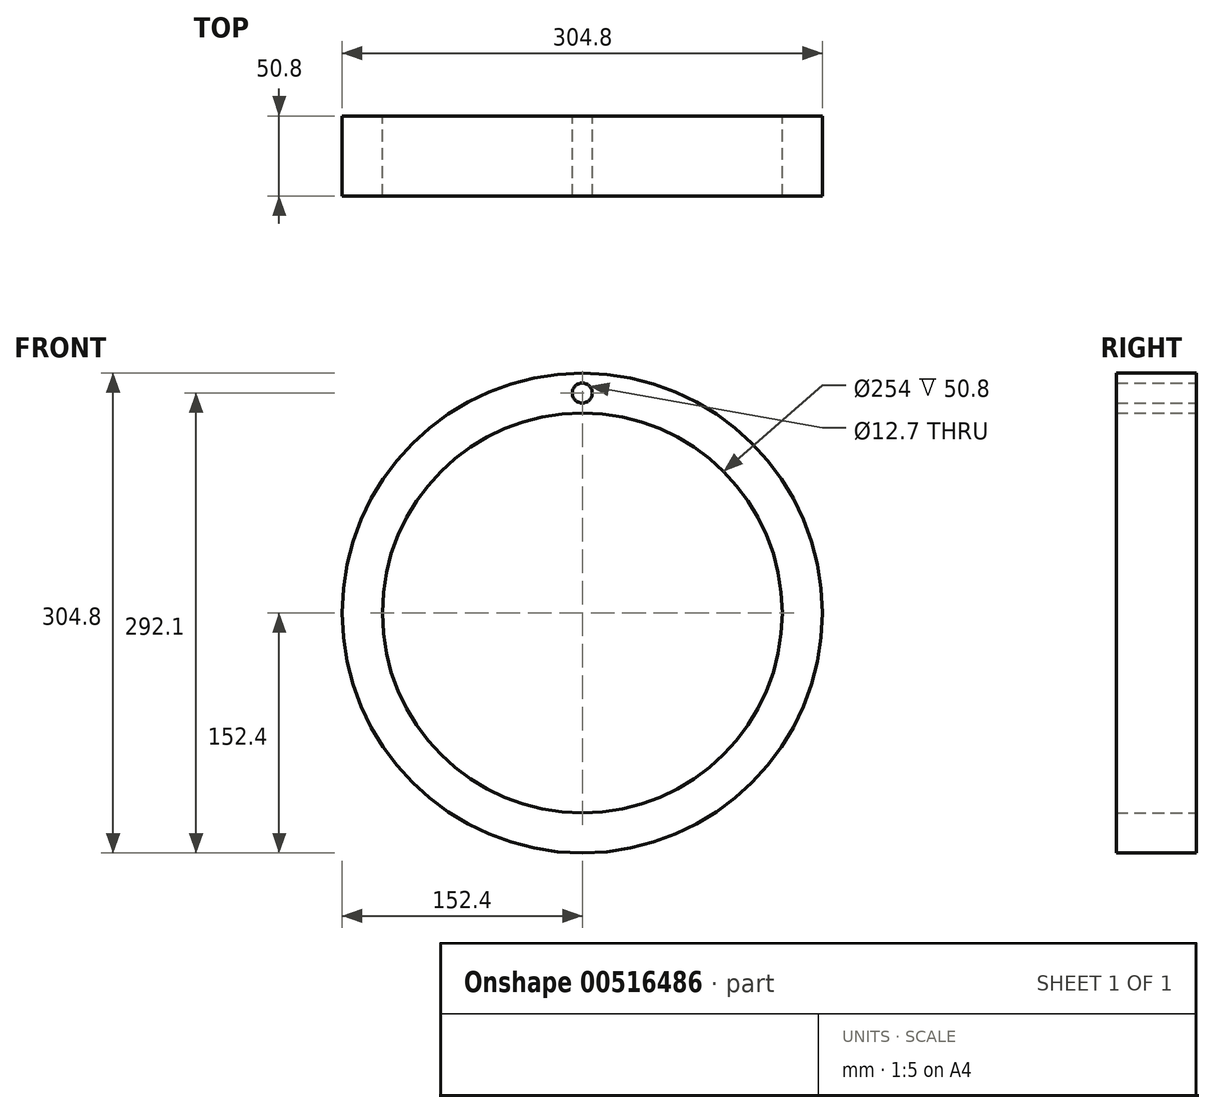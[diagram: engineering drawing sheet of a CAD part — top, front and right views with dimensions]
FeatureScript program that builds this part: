
annotation { "Feature Type Name" : "Feature", "Feature Type Description" : "" }
export const myFeature = defineFeature(function(context is Context, id is Id, definition is map)
    precondition{}
    {
        {
            var Q0;
            Q0=qCreatedBy(makeId("Front.planeOp"),FACE);
            var sketch = newSketch(context, id + "F0", { "sketchPlane" : qUnion([Q0])});
            skCircle(sketch, "E0", {"center": v(0, 0) * mm, "radius": 152.4 * mm});
            skCircle(sketch, "E1", {"center": v(0, 0) * mm, "radius": 127 * mm});
            skCircle(sketch, "E2", {"center": v(0, 139.7) * mm, "radius": 6.35 * mm});
            skSolve(sketch);
        }
        {
            var Q0;
            Q0=makeQuery(id+"F0.imprint","IMPRINT",FACE,{"disambiguationData":[TD([[makeQuery(id+"F0.imprint","IMPRINT",EDGE,{"derivedFrom":sQuery(id+"F0.wireOp",EDGE,"E0")}),1.0]])]});
            extrude(context, id + "F1", {"entities" : qUnion([Q0]), "depth" : 50.8 * mm, "offsetDistance" : 25.4 * mm});
        }
    });
